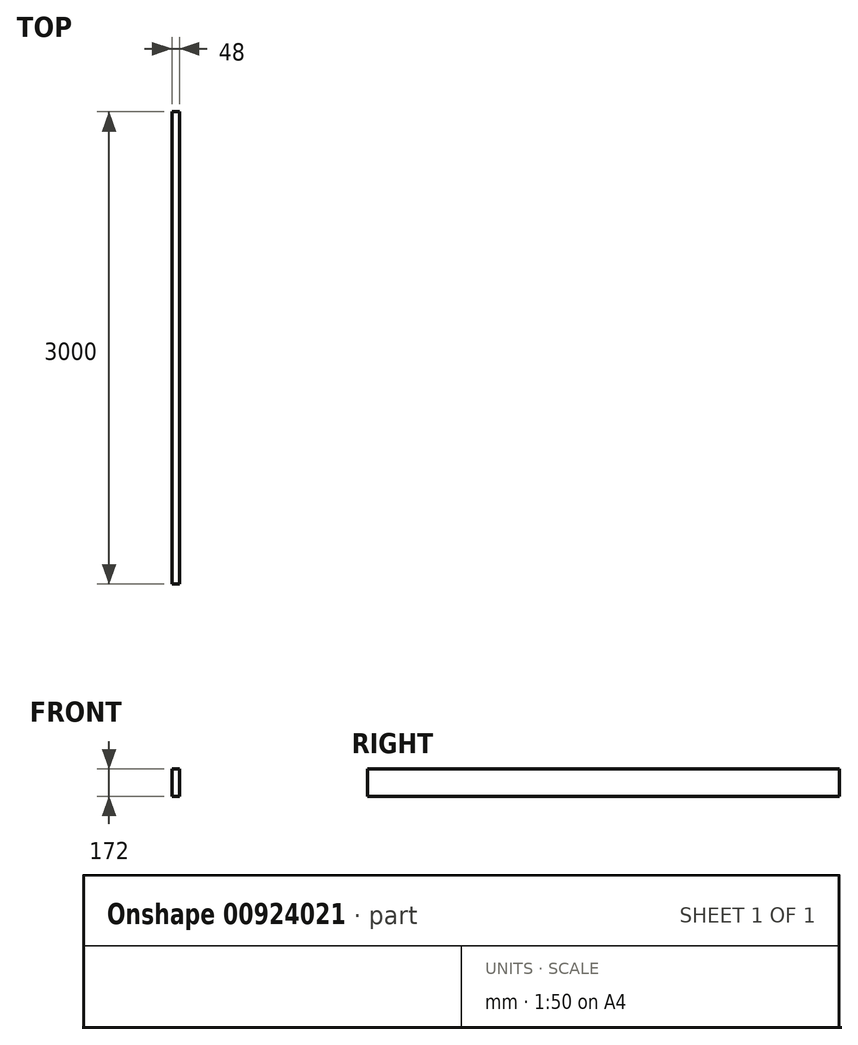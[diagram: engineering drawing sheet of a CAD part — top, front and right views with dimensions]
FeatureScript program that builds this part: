
annotation { "Feature Type Name" : "Feature", "Feature Type Description" : "" }
export const myFeature = defineFeature(function(context is Context, id is Id, definition is map)
    precondition{}
    {
        {
            var Q0;
            Q0=qCreatedBy(makeId("Front.planeOp"),FACE);
            var sketch = newSketch(context, id + "F0", { "sketchPlane" : qUnion([Q0])});
            skLineSegment(sketch, "E0.bottom", {"start": v(0, 0) * mm, "end": v(-48, 0) * mm});
            skLineSegment(sketch, "E0.top", {"start": v(0, -172) * mm, "end": v(-48, -172) * mm});
            skLineSegment(sketch, "E0.left", {"start": v(0, 0) * mm, "end": v(0, -172) * mm});
            skLineSegment(sketch, "E0.right", {"start": v(-48, 0) * mm, "end": v(-48, -172) * mm});
            skSolve(sketch);
        }
        {
            var Q0;
            Q0=qSketchRegion(id+"F0",true);
            extrude(context, id + "F1", {"entities" : qUnion([Q0]), "depth" : 3000 * mm, "offsetDistance" : 25 * mm});
        }
    });
